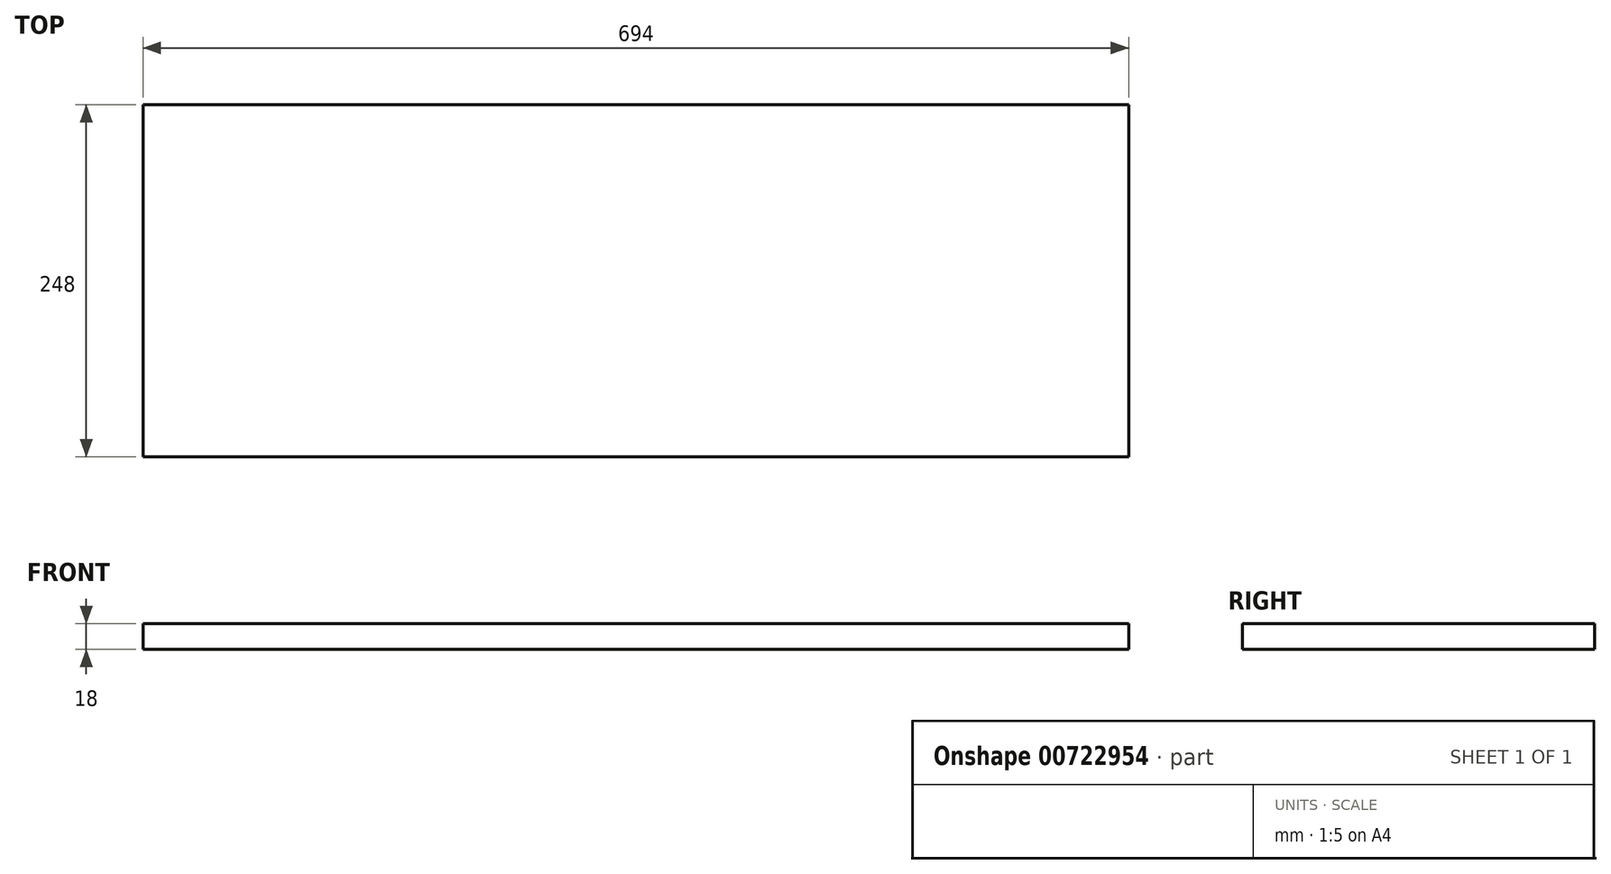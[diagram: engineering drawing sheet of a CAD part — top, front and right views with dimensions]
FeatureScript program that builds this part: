
annotation { "Feature Type Name" : "Feature", "Feature Type Description" : "" }
export const myFeature = defineFeature(function(context is Context, id is Id, definition is map)
    precondition{}
    {
        {
            var Q0;
            Q0=qCreatedBy(makeId("Top.planeOp"),FACE);
            var sketch = newSketch(context, id + "F0", { "sketchPlane" : qUnion([Q0])});
            skLineSegment(sketch, "E0.bottom", {"start": v(-314.08, -149.4) * mm, "end": v(379.92, -149.4) * mm});
            skLineSegment(sketch, "E0.top", {"start": v(-314.08, -397.4) * mm, "end": v(379.92, -397.4) * mm});
            skLineSegment(sketch, "E0.left", {"start": v(-314.08, -149.4) * mm, "end": v(-314.08, -397.4) * mm});
            skLineSegment(sketch, "E0.right", {"start": v(379.92, -149.4) * mm, "end": v(379.92, -397.4) * mm});
            skLineSegment(sketch, "E1", {"start": v(-314.08, -149.4) * mm, "end": v(379.92, -397.4) * mm, "construction": true});
            skLineSegment(sketch, "E2", {"start": v(379.92, -149.4) * mm, "end": v(-314.08, -397.4) * mm, "construction": true});
            skSolve(sketch);
        }
        {
            var Q0;
            Q0 = qSketchRegion(id + "F0", true);
            extrude(context, id + "F1", {"entities" : qUnion([Q0]), "depth" : 18 * mm, "offsetDistance" : 25 * mm});
        }
    });
